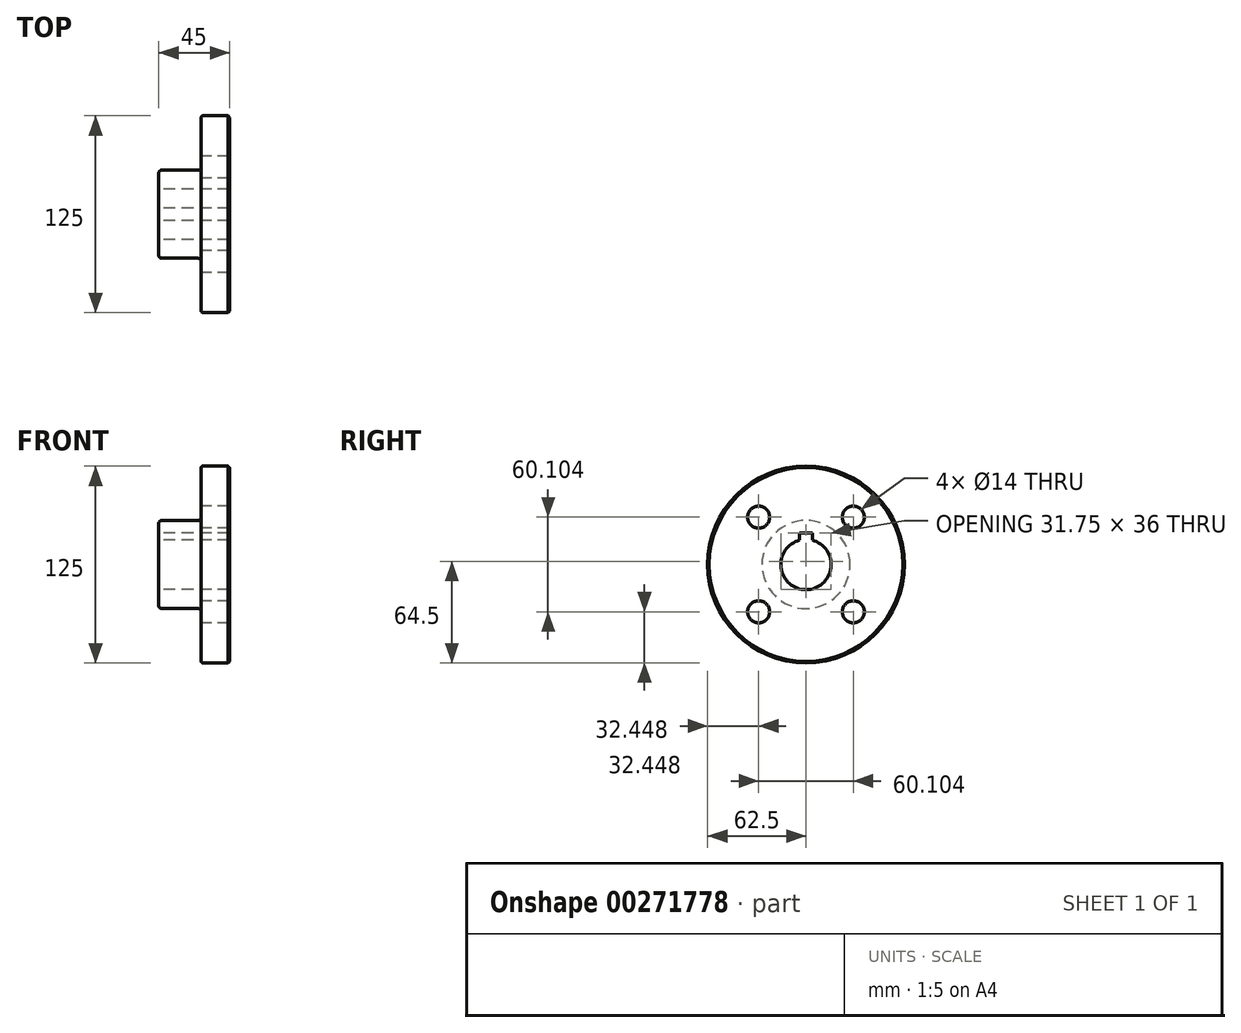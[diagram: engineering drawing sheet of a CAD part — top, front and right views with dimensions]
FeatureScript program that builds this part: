
annotation { "Feature Type Name" : "Feature", "Feature Type Description" : "" }
export const myFeature = defineFeature(function(context is Context, id is Id, definition is map)
    precondition{}
    {
        {
            var Q0;
            Q0=qCreatedBy(makeId("Front.planeOp"),FACE);
            var sketch = newSketch(context, id + "F0", { "sketchPlane" : qUnion([Q0])});
            skLineSegment(sketch, "E0", {"start": v(0, 16) * mm, "end": v(0, 62.5) * mm});
            skLineSegment(sketch, "E1", {"start": v(0, 62.5) * mm, "end": v(-18, 62.5) * mm});
            skLineSegment(sketch, "E2", {"start": v(-18, 62.5) * mm, "end": v(-18, 28) * mm});
            skLineSegment(sketch, "E3", {"start": v(-18, 28) * mm, "end": v(-45, 28) * mm});
            skLineSegment(sketch, "E4", {"start": v(-45, 28) * mm, "end": v(-45, 16) * mm});
            skLineSegment(sketch, "E5", {"start": v(-61.5, 0) * mm, "end": v(24.65, 0) * mm, "construction": true});
            skLineSegment(sketch, "E6", {"start": v(-45, 16) * mm, "end": v(0, 16) * mm});
            skSolve(sketch);
        }
        {
            var Q0;
            Q0=makeQuery(id+"F0.imprint","IMPRINT",FACE,{"disambiguationData":[TD([[makeQuery(id+"F0.imprint","IMPRINT",EDGE,{"derivedFrom":sQuery(id+"F0.wireOp",EDGE,"E0")}),1.0]])]});
            var Q1;
            Q1=sQuery(id+"F0.wireOp",EDGE,"E5");
            revolve(context, id + "F1", {"entities" : qUnion([Q0]), "axis" : qUnion([Q1]), "revolveType" : RevolveType.FULL});
        }
        {
            var Q0;
            Q0=makeQuery(id+"F1.opRevolve","SWEPT_FACE",FACE,{"disambiguationData":[OSD([sQuery(id+"F0.wireOp",EDGE,"E4")])]});
            var sketch = newSketch(context, id + "F2", { "sketchPlane" : qUnion([Q0])});
            skLineSegment(sketch, "E7.bottom", {"start": v(-4, 20) * mm, "end": v(4, 20) * mm});
            skLineSegment(sketch, "E7.top", {"start": v(-4, 12) * mm, "end": v(4, 12) * mm});
            skLineSegment(sketch, "E7.left", {"start": v(-4, 20) * mm, "end": v(-4, 12) * mm});
            skLineSegment(sketch, "E7.right", {"start": v(4, 20) * mm, "end": v(4, 12) * mm});
            skSolve(sketch);
        }
        {
            var Q0;
            Q0 = qSketchRegion(id + "F2", true);
            extrude(context, id + "F3", {"entities" : qUnion([Q0]), "operationType" : NewBodyOperationType.REMOVE, "endBound" : BoundingType.THROUGH_ALL, "oppositeDirection" : true, "depth" : 25 * mm});
        }
        {
            var Q0;
            Q0=makeQuery(id+"F1.opRevolve","SWEPT_FACE",FACE,{"disambiguationData":[OSD([sQuery(id+"F0.wireOp",EDGE,"E2")])]});
            var sketch = newSketch(context, id + "F4", { "sketchPlane" : qUnion([Q0])});
            skLineSegment(sketch, "E8", {"start": v(0, 0) * mm, "end": v(-30.05, 30.05) * mm, "construction": true});
            skLineSegment(sketch, "E9.MirrorCS", {"start": v(0, 0) * mm, "end": v(30.05, 30.05) * mm, "construction": true});
            skLineSegment(sketch, "E10.MirrorCS", {"start": v(0, 0) * mm, "end": v(30.05, -30.05) * mm, "construction": true});
            skLineSegment(sketch, "E11.MirrorCS", {"start": v(0, 0) * mm, "end": v(-30.05, -30.05) * mm, "construction": true});
            skSolve(sketch);
        }
        {
            var Q0;
            Q0=sQuery(id+"F4.wireOp",VERTEX,"E8.end");
            var Q1;
            Q1=sQuery(id+"F4.wireOp",VERTEX,"E11.MirrorCS.end");
            var Q2;
            Q2=sQuery(id+"F4.wireOp",VERTEX,"E10.MirrorCS.end");
            var Q3;
            Q3=sQuery(id+"F4.wireOp",VERTEX,"E9.MirrorCS.end");
            var Q4;
            Q4=makeQuery(id+"F1.opRevolve","SWEPT_BODY",BODY,{"disambiguationData":[OSD([sQuery(id+"F0.wireOp",EDGE,"E0"),sQuery(id+"F0.wireOp",EDGE,"E1"),sQuery(id+"F0.wireOp",EDGE,"E2"),sQuery(id+"F0.wireOp",EDGE,"E3"),sQuery(id+"F0.wireOp",EDGE,"E4"),sQuery(id+"F0.wireOp",EDGE,"E6")])]});
            hole(context, id + "F5", {"style" : HoleStyle.SIMPLE, "endStyle" : HoleEndStyle.THROUGH, "holeDiameter" : 14 * mm, "tappedDepth" : 12 * mm, "tapClearance" : 3, "locations" : qUnion([Q0, Q1, Q2, Q3]), "scope" : qUnion([Q4])});
        }
        {
            var Q0;
            Q0=makeQuery(id+"F1.opRevolve","SWEPT_EDGE",EDGE,{"disambiguationData":[OSD([sQuery(id+"F0.wireOp",EDGE,"E3"),sQuery(id+"F0.wireOp",EDGE,"E4")])]});
            var Q1;
            Q1=makeQuery(id+"F1.opRevolve","SWEPT_EDGE",EDGE,{"disambiguationData":[OSD([sQuery(id+"F0.wireOp",EDGE,"E2"),sQuery(id+"F0.wireOp",EDGE,"E3")])]});
            fillet(context, id + "F6", {"entities" : qUnion([Q0, Q1]), "radius" : 2 * mm, "tangentPropagation" : true, "allowEdgeOverflow" : false});
        }
        {
            var Q0;
            Q0=makeQuery(id+"F1.opRevolve","SWEPT_EDGE",EDGE,{"disambiguationData":[OSD([sQuery(id+"F0.wireOp",EDGE,"E1"),sQuery(id+"F0.wireOp",EDGE,"E2")])]});
            fillet(context, id + "F7", {"entities" : qUnion([Q0]), "radius" : 1 * mm, "tangentPropagation" : true, "allowEdgeOverflow" : false});
        }
        {
            var Q0;
            Q0=makeQuery(id+"F1.opRevolve","SWEPT_EDGE",EDGE,{"disambiguationData":[OSD([sQuery(id+"F0.wireOp",EDGE,"E0"),sQuery(id+"F0.wireOp",EDGE,"E1")])]});
            chamfer(context, id + "F8", {"entities" : qUnion([Q0]), "width" : 1 * mm, "tangentPropagation" : true});
        }
    });
